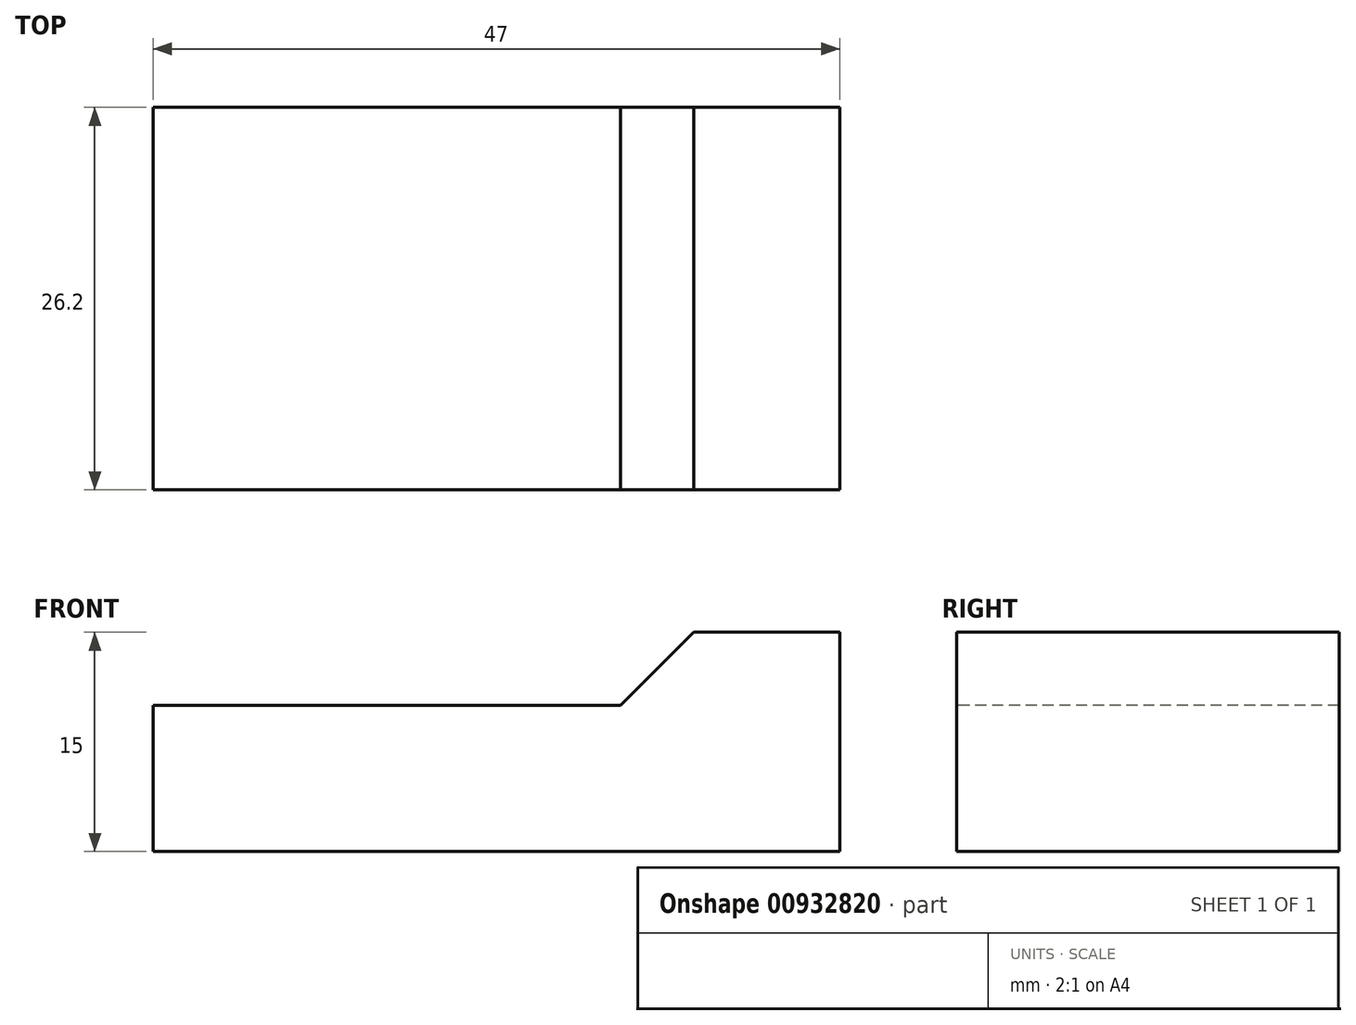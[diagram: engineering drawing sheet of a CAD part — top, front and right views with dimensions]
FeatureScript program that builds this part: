
annotation { "Feature Type Name" : "Feature", "Feature Type Description" : "" }
export const myFeature = defineFeature(function(context is Context, id is Id, definition is map)
    precondition{}
    {
        {
            var Q0;
            Q0=qCreatedBy(makeId("Top.planeOp"),FACE);
            var sketch = newSketch(context, id + "F0", { "sketchPlane" : qUnion([Q0])});
            skLineSegment(sketch, "E0.bottom", {"start": v(-23.5, 13.1) * mm, "end": v(23.5, 13.1) * mm});
            skLineSegment(sketch, "E0.top", {"start": v(-23.5, -13.1) * mm, "end": v(23.5, -13.1) * mm});
            skLineSegment(sketch, "E0.left", {"start": v(-23.5, 13.1) * mm, "end": v(-23.5, -13.1) * mm});
            skLineSegment(sketch, "E0.right", {"start": v(23.5, 13.1) * mm, "end": v(23.5, -13.1) * mm});
            skPoint(sketch, "E0.middle", {"position": v(0, 0) * mm});
            skSolve(sketch);
        }
        {
            var Q0;
            Q0=makeQuery(id+"F0.imprint","IMPRINT",FACE,{"disambiguationData":[TD([[makeQuery(id+"F0.imprint","IMPRINT",EDGE,{"derivedFrom":sQuery(id+"F0.wireOp",EDGE,"E0.bottom")}),-1.0]])]});
            extrude(context, id + "F1", {"entities" : qUnion([Q0]), "depth" : 15 * mm});
        }
        {
            var Q0;
            Q0=makeQuery(id+"F1.opExtrude","SWEPT_FACE",FACE,{"disambiguationData":[OSD([sQuery(id+"F0.wireOp",EDGE,"E0.top")])]});
            var sketch = newSketch(context, id + "F2", { "sketchPlane" : qUnion([Q0])});
            skLineSegment(sketch, "E1", {"start": v(13.5, 15) * mm, "end": v(8.5, 10) * mm});
            skLineSegment(sketch, "E2", {"start": v(8.5, 10) * mm, "end": v(-23.5, 10) * mm});
            skLineSegment(sketch, "E3", {"start": v(-23.5, 10) * mm, "end": v(-23.5, 15) * mm});
            skLineSegment(sketch, "E4", {"start": v(-23.5, 15) * mm, "end": v(13.5, 15) * mm});
            skSolve(sketch);
        }
        {
            var Q0;
            Q0=makeQuery(id+"F2.imprint","IMPRINT",FACE,{"disambiguationData":[TD([[makeQuery(id+"F2.imprint","IMPRINT",EDGE,{"derivedFrom":sQuery(id+"F2.wireOp",EDGE,"E1")}),-1.0]])]});
            extrude(context, id + "F3", {"entities" : qUnion([Q0]), "operationType" : NewBodyOperationType.REMOVE, "endBound" : BoundingType.THROUGH_ALL, "oppositeDirection" : true, "depth" : 25 * mm});
        }
    });
